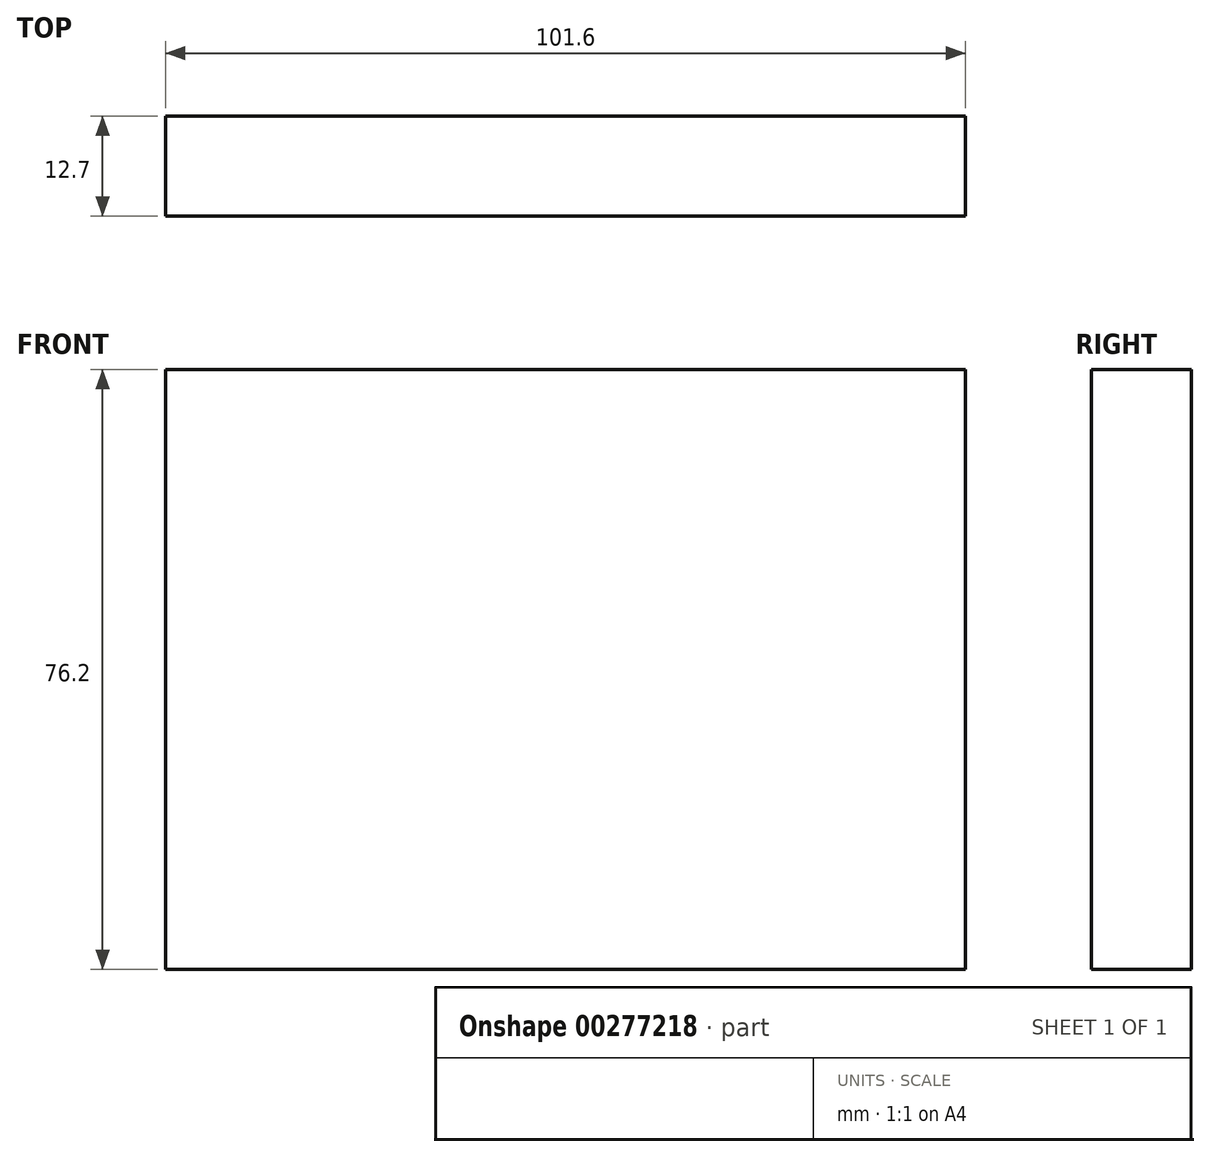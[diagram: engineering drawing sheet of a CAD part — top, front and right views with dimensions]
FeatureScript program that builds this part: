
annotation { "Feature Type Name" : "Feature", "Feature Type Description" : "" }
export const myFeature = defineFeature(function(context is Context, id is Id, definition is map)
    precondition{}
    {
        {
            var Q0;
            Q0=qCreatedBy(makeId("Front.planeOp"),FACE);
            var sketch = newSketch(context, id + "F0", { "sketchPlane" : qUnion([Q0])});
            skLineSegment(sketch, "E0.bottom", {"start": v(0, 0) * mm, "end": v(101.6, 0) * mm});
            skLineSegment(sketch, "E0.top", {"start": v(0, 76.2) * mm, "end": v(101.6, 76.2) * mm});
            skLineSegment(sketch, "E0.left", {"start": v(0, 0) * mm, "end": v(0, 76.2) * mm});
            skLineSegment(sketch, "E0.right", {"start": v(101.6, 0) * mm, "end": v(101.6, 76.2) * mm});
            skSolve(sketch);
        }
        {
            var Q0;
            Q0 = qSketchRegion(id + "F0", true);
            extrude(context, id + "F1", {"entities" : qUnion([Q0]), "depth" : 12.7 * mm});
        }
    });
